# Revit family: Haworth_Executive_Table_SpecialRacetrack
name_source: partatom
category: Furniture Systems
revit_build: Autodesk Revit 2018 (Build: 20170223_1515(x64)
units: mm (PartAtom-declared; Revit-internal decimal feet)

## family parameters
Always vertical = Yes
Cut with Voids When Loaded = No
OmniClass Number = 23.40.70.14.64.21
OmniClass Title = Systems Furniture
Part Type = Normal
Room Calculation Point = No
Round Connector Dimension = Use Diameter
Shared = No
Work Plane-Based = No

## types (5) — shared parameters
Actual Depth = 48"
Actual Height = 29 1/2"
Assembly Code = E2020200
Border = Yes
Border Offset = 4 1/2"
Flip Top Finish = Haworth - Paint - Metallic Champagne
Manufacturer = Haworth
Model = Haworth_Executive-Table-Ractrack_Special
Revision Number = 1
Size = Verify Final Dim. w/ Haworth
Standard Depths = 36, 42, 48, 54, 60 in.
Support Finish = Haworth - Wood - Mahogany
Sustainability = http://haworth.com
Top Edge Finish = Haworth - Wood - Mahogany
Top Finish = Haworth - Wood - Mahogany
Top Thickness = 1 1/2"
URL = http://haworth.com
URL - Product = http://haworth.com
Warranty = http://haworth.com
Width = 96"

## per-type parameters (varying)
| type | Actual Width | Base Kit Full Cylinder | Base Kit Half Cylinder | Base Kit Wood Slab | Base Kit Wood X | Cylinder Size | Depth 36 | Depth 42 | Depth 48 | Depth 54 | Depth 60 | Description | Max Width | Min Width | Slab Width | Standard Widths | Support Offset | Wood X Size |
| 60d 120w Slab Base | 108" | No | No | Yes | No | 30" | No | No | No | No | Yes | Haworth_Executive-Table-Rectangle_One-Piece | 120" | 108" | 60" | 108, 120 in. | 30" | 32" |
| 54d 120w X Bases | 108" | No | No | No | Yes | 24" | No | No | No | Yes | No | Haworth_Executive-Table-Rectangle_One-Piece | 120" | 108" | 60" | 108, 120 in. | 27" | 26" |
| 48d 96w Half Cylinder Bases | 96" | No | Yes | No | No | 24" | No | No | Yes | No | No | Haworth_Executive-Table-Ractrack_Special | 120" | 84" | 48" | 84, 96, 108, 120 in. | 24" | 26" |
| 42d 96w Full Cylinder Bases | 96" | Yes | No | No | No | 18" | No | Yes | No | No | No | Haworth_Executive-Table-Rectangle_One-Piece | 120" | 78" | 48" | 78, 84, 96, 108, 120 in. | 21" | 26" |
| 36d 72w Slab Base | 84" | No | No | Yes | No | 18" | Yes | No | No | No | No | Haworth_Executive-Table-Rectangle_One-Piece | 84" | 60" | 36" | 60, 66, 72, 78, 84 in. | 18" | 26" |

## geometry (parser evidence)
native form markers: Blend x4, Sweep x11
no freeform markers — native parametric forms only
